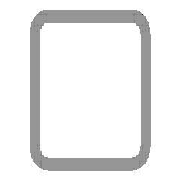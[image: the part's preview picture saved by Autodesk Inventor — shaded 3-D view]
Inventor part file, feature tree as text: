
AUTODESK INVENTOR PART (.ipt)
format: ipt  version: 2025 (Build 290162010, 162A)  size: 134,656 bytes
history: native  units: mm (DEFAULTED — no unit token found)
features: other x4, sketch x1, plane x1
ambient origin geometry x8: Origin, YZ Plane, XZ Plane, XY Plane, X Axis, Y Axis, Z Axis, Center Point
bodies: Solid1 (feature_tree), Body (feature_tree)
feature tree (6):
  parser-record x1  (decoder bookkeeping rows leaked as tree rows — omitted from the tree; the rows remain in map.json)
  other  "Driven Length"
  other  "Start Plane"
  other  "End Plane"
  sketch  "Sketch3"  dims[d3=885.375318mm d4=0.0mm d7=6.0mm d9=80.0mm d11=80.0mm d12=3.0mm d13=80.0mm d14=965.375318mm d15=40.0mm d16=40.0mm d17=90.0deg d18=885.375318mm]
  plane  "Work Plane3"
